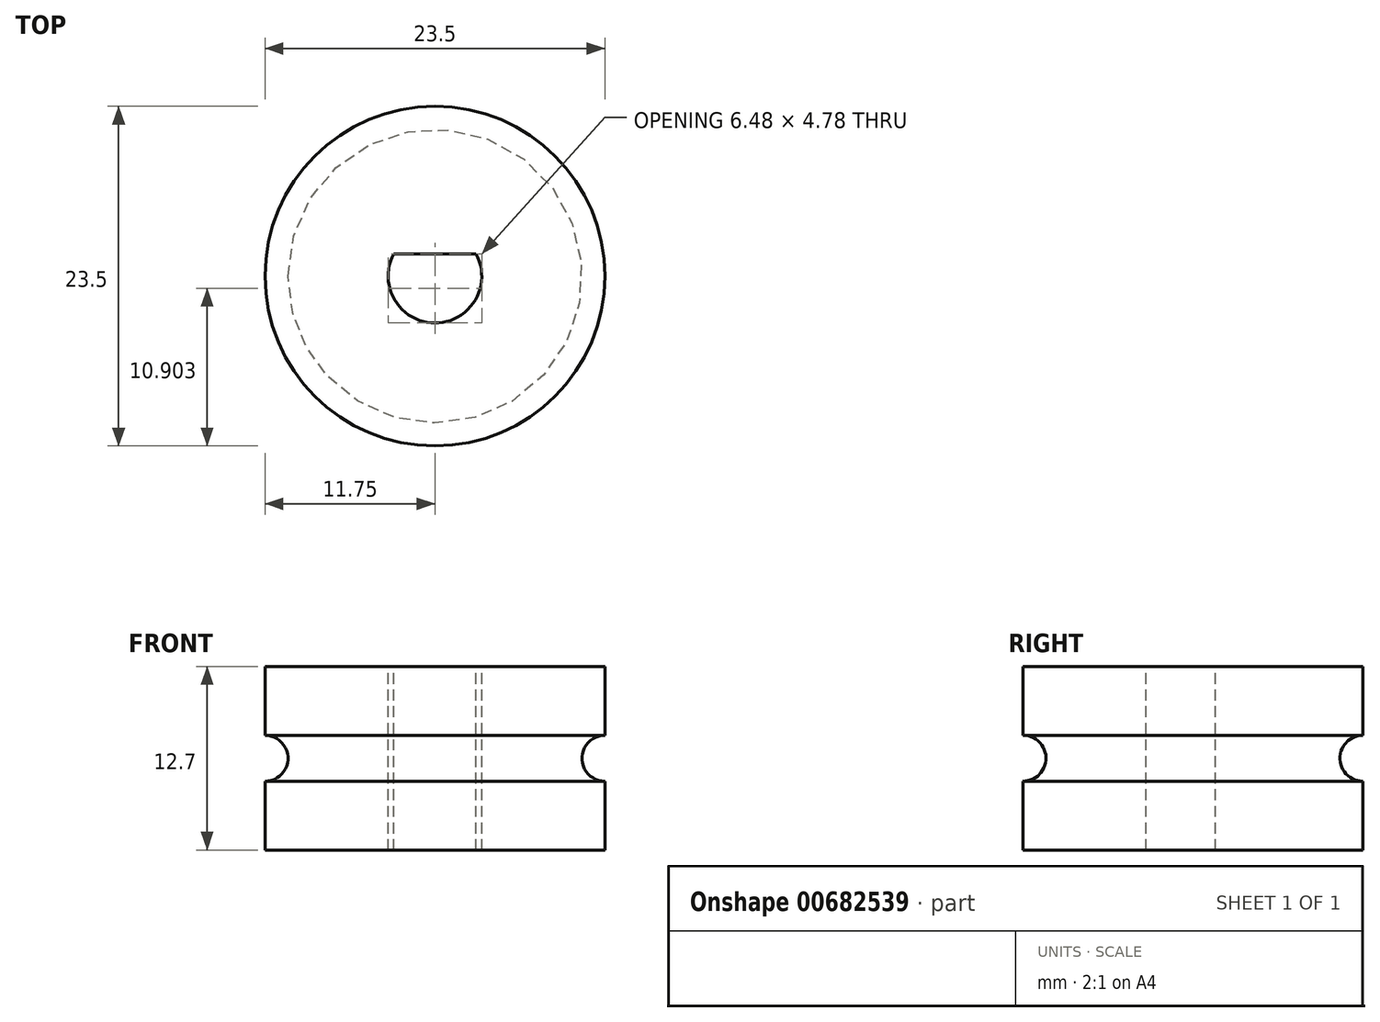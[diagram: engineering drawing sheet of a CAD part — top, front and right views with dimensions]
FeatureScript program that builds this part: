
annotation { "Feature Type Name" : "Feature", "Feature Type Description" : "" }
export const myFeature = defineFeature(function(context is Context, id is Id, definition is map)
    precondition{}
    {
        {
            var Q0;
            Q0=qCreatedBy(makeId("Front.planeOp"),FACE);
            var sketch = newSketch(context, id + "F0", { "sketchPlane" : qUnion([Q0])});
            skLineSegment(sketch, "E0", {"start": v(0, 0) * mm, "end": v(0, 6.35) * mm});
            skLineSegment(sketch, "E1", {"start": v(0, 6.35) * mm, "end": v(-11.75, 6.35) * mm});
            skLineSegment(sketch, "E2", {"start": v(-11.75, 6.35) * mm, "end": v(-11.75, -6.35) * mm});
            skLineSegment(sketch, "E3", {"start": v(-11.75, -6.35) * mm, "end": v(0, -6.35) * mm});
            skLineSegment(sketch, "E4", {"start": v(0, -6.35) * mm, "end": v(0, 0) * mm});
            skCircle(sketch, "E5", {"center": v(-11.75, 0) * mm, "radius": 1.59 * mm});
            skSolve(sketch);
        }
        {
            var Q0;
            Q0=makeQuery(id+"F0.imprint","IMPRINT",FACE,{"disambiguationData":[TD([[makeQuery(id+"F0.imprint","IMPRINT",EDGE,{"derivedFrom":sQuery(id+"F0.wireOp",EDGE,"E0")}),1.0]])]});
            var Q1;
            Q1=sQuery(id+"F0.wireOp",EDGE,"E0");
            revolve(context, id + "F1", {"surfaceOperationType" : NewSurfaceOperationType.NEW, "entities" : qUnion([Q0]), "axis" : qUnion([Q1]), "revolveType" : RevolveType.FULL});
        }
        {
            var Q0;
            Q0=makeQuery(id+"F1.opRevolve","SWEPT_FACE",FACE,{"disambiguationData":[OSD([sQuery(id+"F0.wireOp",EDGE,"E1")])]});
            var sketch = newSketch(context, id + "F2", { "sketchPlane" : qUnion([Q0])});
            skCircle(sketch, "E6", {"center": v(0, 0) * mm, "radius": 3.24 * mm});
            skLineSegment(sketch, "E7.0", {"start": v(2.85, 1.54) * mm, "end": v(-2.85, 1.54) * mm});
            skSolve(sketch);
        }
        {
            var Q0;
            {var subQ0=sQuery(id+"F2.wireOp",EDGE,"E7.0");Q0=makeQuery(id+"F2.imprint","IMPRINT",FACE,{"disambiguationData":[TD([[makeQuery(id+"F2.imprint","IMPRINT",EDGE,{"derivedFrom":subQ0}),1.0]])]});}
            extrude(context, id + "F3", {"entities" : qUnion([Q0]), "operationType" : NewBodyOperationType.REMOVE, "endBound" : BoundingType.THROUGH_ALL, "oppositeDirection" : true, "depth" : 25.4 * mm, "offsetDistance" : 25.4 * mm});
        }
    });
